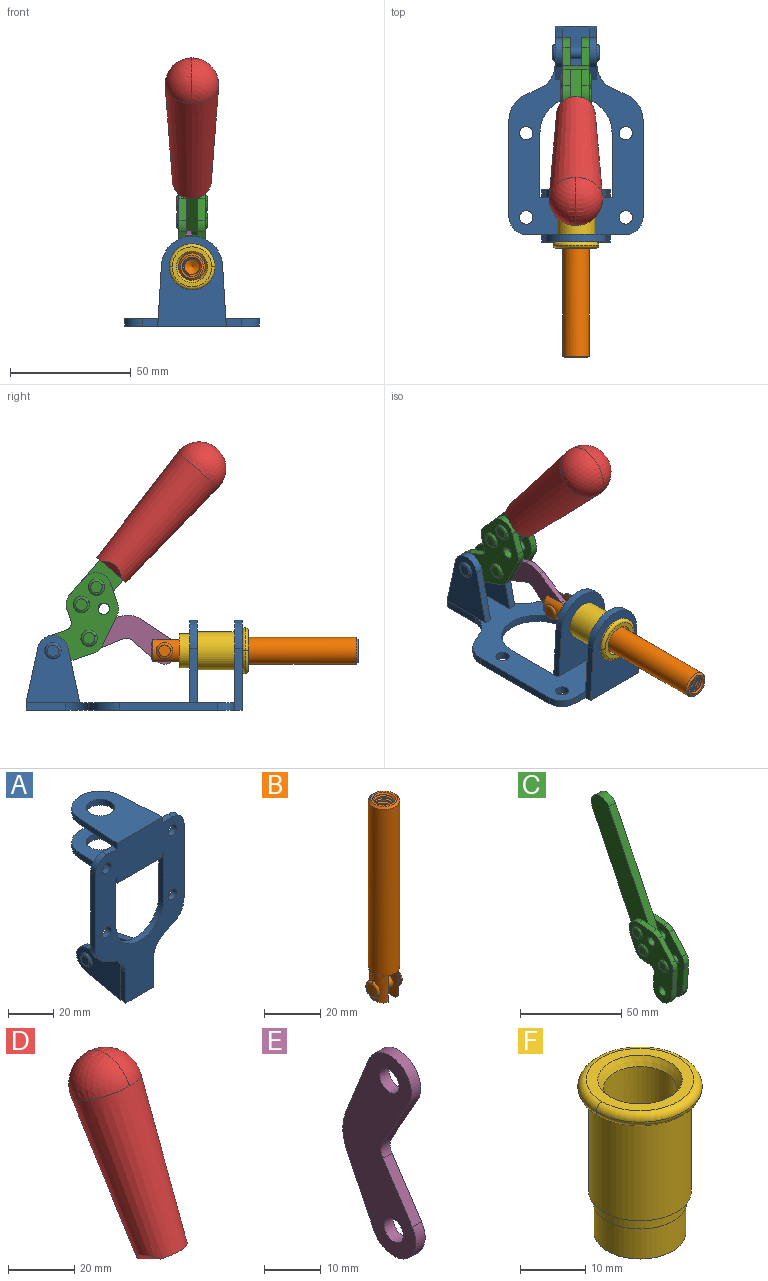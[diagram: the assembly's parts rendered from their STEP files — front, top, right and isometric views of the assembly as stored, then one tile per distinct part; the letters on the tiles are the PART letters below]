
ASSEMBLY  parts=6 mates=6
PART A: 55 faces, bbox 55.7x37.4x89.8 mm
  f0: torus R=2.41mm, axis (-1,0,0), area 15mm2, adj f11,f15,f25
  f1: torus R=2.41mm, axis (-1,0,0), area 15mm2, adj f10,f12,f22
  f2: cylinder r=2.78mm len=5.56mm, axis (0,-1,0), area 54.2mm2, adj f30,f54
  f3: cylinder r=14.99mm len=29.97mm, axis (0,-1,0), area 145.9mm2, adj f30,f49,f53,f54
  f4: cylinder r=2.78mm len=5.56mm, axis (0,-1,0), area 54.2mm2, adj f30,f54
  f5: cylinder r=2.78mm len=5.56mm, axis (0,-1,0), area 54.2mm2, adj f30,f54
  f6: cylinder r=2.78mm len=5.56mm, axis (0,-1,0), area 54.2mm2, adj f30,f54
  f7: cylinder r=6.35mm len=12.7mm, axis (0,0,1), area 123.6mm2, adj f27,f51
  f8: cylinder r=6.35mm len=12.7mm, axis (0,0,-1), area 124.7mm2, adj f21,f35
  f9: cylinder r=2.41mm len=11.18mm, axis (-1,0,0), area 169.4mm2, adj f16,f19
  f10: plane 4.83x4.83mm, normal (1,0,0), area 18.3mm2, adj f1,f12
  f11: plane 4.83x4.83mm, normal (-1,0,0), area 18.3mm2, adj f0,f15
  f12: torus R=2.41mm, axis (-1,0,0), area 15mm2, adj f1,f10,f22
  f13: cylinder r=6.35mm len=12.41mm, axis (1,0,0), area 53.4mm2, adj f18,f19,f22,f23
  f14: cylinder r=6.35mm len=12.41mm, axis (-1,0,0), area 53.4mm2, adj f16,f17,f24,f25
  f15: torus R=2.41mm, axis (-1,0,0), area 15mm2, adj f0,f11,f25
  f16: plane 27.86x22.35mm, normal (1,0,0), area 425.4mm2, adj f9,f14,f17,f24,f30
  f17: plane 22.86x4.97mm, normal (0,0.21,0.98), area 72.5mm2, adj f14,f16,f25,f30
  f18: plane 22.86x4.97mm, normal (0,0.21,0.98), area 72.5mm2, adj f13,f19,f22,f30
  f19: plane 27.86x22.35mm, normal (-1,0,0), area 425.4mm2, adj f9,f13,f18,f23,f30
  f20: cylinder r=12.7mm len=25.35mm, axis (0,0,-1), area 119.8mm2, adj f21,f34,f35,f36
  f21: plane 34.21x28.07mm, normal (0,0,-1), area 702.4mm2, adj f8,f20,f30,f34,f36
  f22: plane 27.96x22.45mm, normal (1,0,0), area 407.2mm2, adj f1,f12,f13,f18,f23,f30,f42,f43
  f23: plane 22.86x4.97mm, normal (0,0.21,-0.98), area 72.5mm2, adj f13,f19,f22,f44
  f24: plane 22.86x4.97mm, normal (0,0.21,-0.98), area 72.5mm2, adj f14,f16,f25,f44
  f25: plane 27.86x22.35mm, normal (-1,0,0), area 407.1mm2, adj f0,f14,f15,f17,f24,f30,f45,f46
  f26: plane 3.1x0.95mm, normal (0,0,-1), area 2.7mm2, adj f30,f49,f50,f54
  f27: plane 34.21x28.07mm, normal (0,0,1), area 702.4mm2, adj f7,f28,f30,f50,f52
  f28: cylinder r=12.7mm len=25.35mm, axis (0,0,1), area 118.8mm2, adj f27,f50,f51,f52
  f29: plane 3.1x0.95mm, normal (0,0,-1), area 2.7mm2, adj f30,f52,f53,f54
  f30: plane 86.54x55.63mm, normal (0,1,0), area 2362.9mm2, adj f2,f3,f4,f5,f6,f16,f17,f18
  f31: plane 40.56x3.1mm, normal (-1,0,0), area 125.7mm2, adj f30,f32,f48,f54
  f32: cylinder r=7.11mm len=7.11mm, axis (0,-1,0), area 34.6mm2, adj f30,f31,f33,f54
  f33: plane 6.67x3.1mm, normal (0,0,1), area 20.4mm2, adj f30,f32,f34,f54
  f34: plane 25.39x3.13mm, normal (-1,0.06,0), area 79.5mm2, adj f20,f21,f33,f35,f54
  f35: plane 37.31x28.45mm, normal (0,0,1), area 789.9mm2, adj f8,f20,f34,f36,f54
  f36: plane 25.39x3.13mm, normal (1,0.06,0), area 79.5mm2, adj f20,f21,f35,f37,f54
  f37: plane 6.67x3.1mm, normal (0,0,1), area 20.4mm2, adj f30,f36,f38,f54
  f38: cylinder r=7.11mm len=7.11mm, axis (0,-1,0), area 34.6mm2, adj f30,f37,f39,f54
  f39: plane 40.56x3.1mm, normal (1,0,0), area 125.7mm2, adj f30,f38,f40,f54
  f40: cylinder r=11.18mm len=10.16mm, axis (0,-1,0), area 39.5mm2, adj f30,f39,f41,f54
  f41: plane 6.09x3.1mm, normal (0.42,0,-0.91), area 20.8mm2, adj f30,f40,f42,f54
  f42: cylinder r=11.18mm len=9.41mm, axis (0,-1,0), area 37.2mm2, adj f22,f30,f41,f43,f54
  f43: plane 16.5x3.1mm, normal (1,0,0), area 51.1mm2, adj f22,f42,f44,f54
  f44: plane 17.37x3.1mm, normal (0,0,-1), area 53.8mm2, adj f23,f24,f30,f43,f45,f54
  f45: plane 16.5x3.1mm, normal (-1,0,0), area 51.1mm2, adj f25,f44,f46,f54
  f46: cylinder r=11.18mm len=9.41mm, axis (0,-1,0), area 37.2mm2, adj f25,f30,f45,f47,f54
  f47: plane 6.09x3.1mm, normal (-0.42,0,-0.91), area 20.8mm2, adj f30,f46,f48,f54
  f48: cylinder r=11.18mm len=10.16mm, axis (0,-1,0), area 39.5mm2, adj f30,f31,f47,f54
  f49: plane 26.54x3.1mm, normal (-1,0,0), area 82.3mm2, adj f3,f26,f30,f54
  f50: plane 25.39x3.1mm, normal (1,0.06,0), area 78.8mm2, adj f26,f27,f28,f51,f54
  f51: plane 37.31x28.45mm, normal (0,0,-1), area 789.9mm2, adj f7,f28,f50,f52,f54
  f52: plane 25.39x3.1mm, normal (-1,0.06,0), area 78.8mm2, adj f27,f28,f29,f51,f54
  f53: plane 26.54x3.1mm, normal (1,0,0), area 82.3mm2, adj f3,f29,f30,f54
  f54: plane 89.66x55.63mm, normal (0,-1,0), area 2678.5mm2, adj f2,f3,f4,f5,f6,f26,f29,f31
PART B: 48 faces, bbox 12.6x11.1x86.1 mm
  f0: torus R=2.41mm, axis (-1,0,0), area 15mm2, adj f30,f32,f34
  f1: torus R=2.41mm, axis (-1,0,0), area 15mm2, adj f29,f31,f33
  f2: cylinder r=5.54mm len=72.39mm, axis (0,0,1), area 2518.5mm2, adj f3,f4,f42,f43
  f3: cone r=5.54mm half-angle=45deg, axis (0,0,1), area 7.6mm2, adj f2,f5,f41
  f4: cone r=5.54mm half-angle=45deg, axis (0,0,-1), area 34.9mm2, adj f2,f39
  f5: cylinder r=5.08mm len=11.48mm, axis (0,0,1), area 108.3mm2, adj f3,f7,f8,f41
  f6: cylinder r=2.41mm len=4.83mm, axis (-1,0,0), area 71.2mm2, adj f40,f41
  f7: cylinder r=2.41mm len=4.83mm, axis (-1,0,0), area 7.6mm2, adj f5,f34
  f8: cone r=5.08mm half-angle=45deg, axis (0,0,1), area 10.6mm2, adj f5,f37,f41
  f9: cone r=3.98mm half-angle=45deg, axis (0,0,1), area 17.6mm2, adj f27,f39,f45,f46,f47
  f10: cylinder r=2.41mm len=4.83mm, axis (-1,0,0), area 7.6mm2, adj f33,f38
  f11: cylinder r=3.2mm len=6.4mm, axis (0,0,1), area 78.4mm2, adj f12,f28,f44,f45,f47
  f12: cylinder r=3.2mm len=6.4mm, axis (0,0,1), area 10.5mm2, adj f11,f13,f45,f47
  f13: cylinder r=3.2mm len=6.4mm, axis (0,0,1), area 10.5mm2, adj f12,f14,f45,f47
  f14: cylinder r=3.2mm len=6.4mm, axis (0,0,1), area 10.5mm2, adj f13,f15,f45,f47
  f15: cylinder r=3.2mm len=6.4mm, axis (0,0,1), area 10.5mm2, adj f14,f16,f45,f47
  f16: cylinder r=3.2mm len=6.4mm, axis (0,0,1), area 10.5mm2, adj f15,f17,f45,f47
  f17: cylinder r=3.2mm len=6.4mm, axis (0,0,1), area 10.5mm2, adj f16,f18,f45,f47
  f18: cylinder r=3.2mm len=6.4mm, axis (0,0,1), area 10.5mm2, adj f17,f19,f45,f47
  f19: cylinder r=3.2mm len=6.4mm, axis (0,0,1), area 10.5mm2, adj f18,f20,f45,f47
  f20: cylinder r=3.2mm len=6.4mm, axis (0,0,1), area 10.5mm2, adj f19,f21,f45,f47
  f21: cylinder r=3.2mm len=6.4mm, axis (0,0,1), area 10.5mm2, adj f20,f22,f45,f47
  f22: cylinder r=3.2mm len=6.4mm, axis (0,0,1), area 10.5mm2, adj f21,f23,f45,f47
  f23: cylinder r=3.2mm len=6.4mm, axis (0,0,1), area 10.5mm2, adj f22,f24,f45,f47
  f24: cylinder r=3.2mm len=6.4mm, axis (0,0,1), area 10.5mm2, adj f23,f25,f45,f47
  f25: cylinder r=3.2mm len=6.4mm, axis (0,0,1), area 10.5mm2, adj f24,f26,f45,f47
  f26: cylinder r=3.2mm len=6.4mm, axis (0,0,1), area 10.5mm2, adj f25,f27,f45,f47
  f27: cylinder r=3.2mm len=6.4mm, axis (0,0,1), area 7.4mm2, adj f9,f26,f45,f47
  f28: cone r=3.2mm half-angle=60deg, axis (0,0,1), area 37.2mm2, adj f11
  f29: plane 4.83x4.83mm, normal (-1,0,0), area 18.3mm2, adj f1,f31
  f30: plane 4.83x4.83mm, normal (1,0,0), area 18.3mm2, adj f0,f32
  f31: torus R=2.41mm, axis (-1,0,0), area 15mm2, adj f1,f29,f33
  f32: torus R=2.41mm, axis (-1,0,0), area 15mm2, adj f0,f30,f34
  f33: plane 6.83x6.83mm, normal (1,0,0), area 18.3mm2, adj f1,f10,f31
  f34: plane 6.83x6.83mm, normal (-1,0,0), area 18.3mm2, adj f0,f7,f32
  f35: cone r=5.08mm half-angle=45deg, axis (0,0,1), area 10.6mm2, adj f36,f38,f40
  f36: plane 7.25x1.97mm, normal (0,0,-1), area 10mm2, adj f35,f40
  f37: plane 7.25x1.97mm, normal (0,0,-1), area 10mm2, adj f8,f41
  f38: cylinder r=5.08mm len=11.48mm, axis (0,0,1), area 108.3mm2, adj f10,f35,f40,f42
  f39: plane 9.55x9.55mm, normal (0,0,1), area 22mm2, adj f4,f9
  f40: plane 12.76x10.09mm, normal (1,0,0), area 95.7mm2, adj f6,f35,f36,f38,f42,f43
  f41: plane 12.76x10.09mm, normal (-1,0,0), area 95.7mm2, adj f3,f5,f6,f8,f37,f43
  f42: cone r=5.54mm half-angle=45deg, axis (0,0,1), area 7.6mm2, adj f2,f38,f40
  f43: plane 11.07x4.7mm, normal (0,0,-1), area 50.4mm2, adj f2,f40,f41
  f44: plane 0.89x0.62mm, normal (-1,0,0), area 0.3mm2, adj f11,f45,f46,f47
  f45: bspline ~24.8x7.63mm, area 266.6mm2, adj f9,f11,f12,f13,f14,f15,f16,f17
  f46: bspline ~24.87x7.63mm, area 73.6mm2, adj f9,f44,f45,f47
  f47: bspline ~24.98x7.63mm, area 272.5mm2, adj f9,f11,f12,f13,f14,f15,f16,f17
PART C: 59 faces, bbox 12.9x60.2x99.6 mm
  f0: torus R=2.39mm, axis (-1,0,0), area 14.9mm2, adj f20,f43,f51
  f1: torus R=2.39mm, axis (-1,0,0), area 14.9mm2, adj f19,f42,f51
  f2: torus R=2.39mm, axis (-1,0,0), area 14.9mm2, adj f18,f35,f51
  f3: torus R=2.39mm, axis (-1,0,0), area 14.9mm2, adj f14,f17,f23
  f4: torus R=2.39mm, axis (-1,0,0), area 14.9mm2, adj f13,f16,f23
  f5: torus R=2.39mm, axis (-1,0,0), area 14.9mm2, adj f12,f15,f23
  f6: cylinder r=2.39mm len=4.78mm, axis (1,0,0), area 46.5mm2, adj f48,f50,f51
  f7: cylinder r=2.39mm len=4.78mm, axis (1,0,0), area 46.5mm2, adj f50,f51
  f8: cylinder r=6.35mm len=12.68mm, axis (1,0,0), area 61.8mm2, adj f38,f39,f50,f51
  f9: cylinder r=2.39mm len=4.78mm, axis (-1,0,0), area 70.5mm2, adj f46,f50
  f10: cylinder r=2.39mm len=4.78mm, axis (-1,0,0), area 46.5mm2, adj f23,f45,f46
  f11: cylinder r=2.39mm len=4.78mm, axis (-1,0,0), area 46.5mm2, adj f23,f46
  f12: plane 4.78x4.78mm, normal (1,0,0), area 17.9mm2, adj f5,f15
  f13: plane 4.78x4.78mm, normal (1,0,0), area 17.9mm2, adj f4,f16
  f14: plane 4.78x4.78mm, normal (1,0,0), area 17.9mm2, adj f3,f17
  f15: torus R=2.39mm, axis (-1,0,0), area 14.9mm2, adj f5,f12,f23
  f16: torus R=2.39mm, axis (-1,0,0), area 14.9mm2, adj f4,f13,f23
  f17: torus R=2.39mm, axis (-1,0,0), area 14.9mm2, adj f3,f14,f23
  f18: plane 4.78x4.78mm, normal (-1,0,0), area 17.9mm2, adj f2,f35
  f19: plane 4.78x4.78mm, normal (-1,0,0), area 17.9mm2, adj f1,f42
  f20: plane 4.78x4.78mm, normal (-1,0,0), area 17.9mm2, adj f0,f43
  f21: plane 2.26x0.2mm, normal (1,0,0), area 0.2mm2, adj f31,f44
  f22: plane 2.26x0.2mm, normal (-1,0,0), area 0.2mm2, adj f41,f44
  f23: plane 39.37x30.77mm, normal (1,0,0), area 565.5mm2, adj f3,f4,f5,f10,f11,f15,f16,f17
  f24: cylinder r=6.1mm len=4.15mm, axis (-1,0,0), area 14.7mm2, adj f23,f25,f32,f46
  f25: plane 10.25x9.01mm, normal (0,-0.75,0.66), area 42.3mm2, adj f23,f24,f26,f46
  f26: cylinder r=6.35mm len=4.64mm, axis (-1,0,0), area 15.6mm2, adj f23,f25,f27,f46
  f27: plane 15.84x3.1mm, normal (0,-1,-0.07), area 49.2mm2, adj f23,f26,f28,f46
  f28: cylinder r=6.35mm len=12.68mm, axis (-1,0,0), area 61.8mm2, adj f23,f27,f29,f46
  f29: plane 8.11x3.1mm, normal (0,1,0.07), area 25.2mm2, adj f23,f28,f30,f46
  f30: cylinder r=3.05mm len=3.25mm, axis (-1,0,0), area 14.8mm2, adj f23,f29,f31,f46
  f31: plane 5.99x3.1mm, normal (0,0.07,-1), area 18.6mm2, adj f21,f23,f30,f44,f46
  f32: plane 9.5x3.1mm, normal (0,-0.07,1), area 29.5mm2, adj f23,f24,f33,f46,f47
  f33: cylinder r=6.1mm len=8.63mm, axis (-1,0,0), area 39.1mm2, adj f23,f32,f34,f47
  f34: plane 8.65x3.96mm, normal (0,0.91,-0.42), area 29.5mm2, adj f23,f33,f44,f47
  f35: torus R=2.39mm, axis (-1,0,0), area 14.9mm2, adj f2,f18,f51
  f36: plane 10.25x9.01mm, normal (0,-0.75,0.66), area 42.3mm2, adj f37,f49,f50,f51
  f37: cylinder r=6.35mm len=4.64mm, axis (1,0,0), area 15.6mm2, adj f36,f38,f50,f51
  f38: plane 15.84x3.1mm, normal (0,-1,-0.07), area 49.2mm2, adj f8,f37,f50,f51
  f39: plane 8.11x3.1mm, normal (0,1,0.07), area 25.2mm2, adj f8,f40,f50,f51
  f40: cylinder r=3.05mm len=3.25mm, axis (1,0,0), area 14.8mm2, adj f39,f41,f50,f51
  f41: plane 5.99x3.1mm, normal (0,0.07,-1), area 18.6mm2, adj f22,f40,f44,f50,f51
  f42: torus R=2.39mm, axis (-1,0,0), area 14.9mm2, adj f1,f19,f51
  f43: torus R=2.39mm, axis (-1,0,0), area 14.9mm2, adj f0,f20,f51
  f44: cylinder r=6.35mm len=12.12mm, axis (-1,0,0), area 128.9mm2, adj f21,f22,f23,f31,f34,f41,f46,f47
  f45: plane 2.65x1.35mm, normal (1,0,0), area 1mm2, adj f10,f55
  f46: plane 39.08x20.42mm, normal (-1,0,0), area 412.5mm2, adj f9,f10,f11,f24,f25,f26,f27,f28
  f47: plane 77.62x39.82mm, normal (1,0,0), area 850mm2, adj f32,f33,f34,f44,f53,f54,f55
  f48: plane 2.65x1.35mm, normal (-1,0,0), area 1mm2, adj f6,f55
  f49: cylinder r=6.1mm len=4.15mm, axis (1,0,0), area 14.7mm2, adj f36,f50,f51,f56
  f50: plane 39.08x20.42mm, normal (1,0,0), area 412.5mm2, adj f6,f7,f8,f9,f36,f37,f38,f39
  f51: plane 39.37x30.77mm, normal (-1,0,0), area 565.5mm2, adj f0,f1,f2,f6,f7,f8,f35,f36
  f52: plane 8.65x3.96mm, normal (0,0.91,-0.42), area 29.5mm2, adj f44,f51,f57,f58
  f53: plane 68.49x33.4mm, normal (0,0.9,-0.44), area 358.1mm2, adj f44,f47,f54,f58
  f54: cylinder r=6.35mm len=12.06mm, axis (1,0,0), area 93.7mm2, adj f47,f53,f55,f58
  f55: plane 68.49x33.4mm, normal (0,-0.9,0.44), area 358.1mm2, adj f44,f45,f46,f47,f48,f50,f54,f58
  f56: plane 9.5x3.1mm, normal (0,-0.07,1), area 29.5mm2, adj f49,f50,f51,f57,f58
  f57: cylinder r=6.1mm len=8.63mm, axis (1,0,0), area 39.1mm2, adj f51,f52,f56,f58
  f58: plane 77.62x39.82mm, normal (-1,0,0), area 850mm2, adj f44,f52,f53,f54,f55,f56,f57
PART D: 11 faces, bbox 22.3x42.6x64.5 mm
  f0: sphere r=11.13mm, area 411.4mm2, adj f1,f8
  f1: cone r=11.11mm half-angle=3.3deg, axis (0,0.44,0.9), area 3251.8mm2, adj f0,f7,f8,f9,f10
  f2: cylinder r=6.16mm len=11.7mm, axis (1,0,0), area 89.5mm2, adj f3,f4,f5,f6
  f3: plane 60.23x36.75mm, normal (-1,0,0), area 763.6mm2, adj f2,f4,f6,f10
  f4: plane 51.37x25.05mm, normal (0,0.9,-0.44), area 264.2mm2, adj f2,f3,f5,f10
  f5: plane 60.23x36.75mm, normal (1,0,0), area 763.6mm2, adj f2,f4,f6,f10
  f6: plane 51.37x25.05mm, normal (0,-0.9,0.44), area 264.2mm2, adj f2,f3,f5,f10
  f7: plane 9.95x5.95mm, normal (0.71,-0.31,-0.64), area 25.8mm2, adj f1,f10
  f8: sphere r=11.13mm, area 411.4mm2, adj f0,f1
  f9: plane 9.95x5.95mm, normal (-0.71,-0.31,-0.64), area 25.8mm2, adj f1,f10
  f10: plane 14.27x11.38mm, normal (0,-0.44,-0.9), area 106.7mm2, adj f1,f3,f4,f5,f6,f7,f9
PART E: 12 faces, bbox 2.3x18.2x42.8 mm
  f0: cylinder r=2.4mm len=4.8mm, axis (1,0,0), area 34.9mm2, adj f4,f11
  f1: cylinder r=10.41mm len=8.47mm, axis (1,0,0), area 20.2mm2, adj f4,f9,f10,f11
  f2: cylinder r=3.05mm len=3.16mm, axis (1,0,0), area 7.7mm2, adj f4,f6,f7,f11
  f3: cylinder r=2.4mm len=4.8mm, axis (1,0,0), area 34.9mm2, adj f4,f11
  f4: plane 42.81x18.23mm, normal (-1,0,0), area 414.1mm2, adj f0,f1,f2,f3,f5,f6,f7,f8
  f5: cylinder r=5.54mm len=10.67mm, axis (1,0,0), area 41.8mm2, adj f4,f6,f10,f11
  f6: plane 11.66x6.53mm, normal (0,-0.87,-0.49), area 30.9mm2, adj f2,f4,f5,f11
  f7: plane 11.17x7.33mm, normal (0,-0.84,0.55), area 30.9mm2, adj f2,f4,f8,f11
  f8: cylinder r=5.54mm len=10.51mm, axis (1,0,0), area 41.8mm2, adj f4,f7,f9,f11
  f9: plane 13.67x6.67mm, normal (0,0.9,-0.44), area 35.1mm2, adj f1,f4,f8,f11
  f10: plane 14.1x5.7mm, normal (0,0.93,0.37), area 35.1mm2, adj f1,f4,f5,f11
  f11: plane 42.81x18.23mm, normal (1,0,0), area 414.1mm2, adj f0,f1,f2,f3,f5,f6,f7,f8
PART F: 15 faces, bbox 20.6x20.6x28.7 mm
  f0: torus R=8.26mm, axis (0,0,1), area 56.8mm2, adj f1,f10,f12
  f1: torus R=8.26mm, axis (0,0,1), area 56.8mm2, adj f0,f6,f13
  f2: cylinder r=5.59mm len=25.91mm, axis (0,0,1), area 909.6mm2, adj f3,f4
  f3: cone r=6.86mm half-angle=45deg, axis (0,0,-1), area 70.2mm2, adj f2,f14
  f4: cone r=6.47mm half-angle=30deg, axis (0,0,1), area 66.7mm2, adj f2,f13
  f5: cylinder r=7.04mm len=14.07mm, axis (0,0,1), area 252.6mm2, adj f11,f14
  f6: torus R=8.26mm, axis (0,0,1), area 56.8mm2, adj f1,f12,f13
  f7: cylinder r=7.16mm len=14.33mm, axis (0,0,1), area 91.5mm2, adj f9,f11
  f8: cylinder r=7.86mm len=18.42mm, axis (0,0,1), area 909.6mm2, adj f9,f10
  f9: plane 15.72x15.72mm, normal (0,0,-1), area 33mm2, adj f7,f8
  f10: plane 16.51x16.51mm, normal (0,0,-1), area 19.9mm2, adj f0,f8,f12
  f11: plane 14.33x14.33mm, normal (0,0,-1), area 5.7mm2, adj f5,f7
  f12: torus R=8.26mm, axis (0,0,1), area 56.8mm2, adj f0,f6,f10
  f13: plane 16.51x16.51mm, normal (0,0,1), area 82.7mm2, adj f1,f4,f6
  f14: plane 14.07x14.07mm, normal (0,0,-1), area 7.8mm2, adj f3,f5
PLACE A rot(axis=(1,0,0),90deg) t=(0,9.14,0)mm fixed
PLACE B rot(axis=(1,0,0),90deg) t=(0,10.38,0)mm
PLACE C rot(axis=(1,0,0),66.9deg) t=(0,2.06,14.56)mm
PLACE D rot(axis=(1,0,0),66.9deg) t=(-0.04,2.06,14.56)mm
PLACE E rot(axis=(1,0,0),101.4deg) t=(-1.16,14.95,3.55)mm
PLACE F rot(axis=(1,0,0),90deg) t=(0,9.14,0)mm
MATE fastened F.f0 <-> A.f7  axis (0,1,0) through (0,-37.25,24.61)mm
MATE revolute E.f3 <-> C.f4  axis (1,0,0) through (0,26.23,29.8)mm
MATE slider B.f2 <-> F.f2  axis (0,-1,0) through (0,-48.4,24.61)mm
MATE revolute C.f7 <-> A.f0  axis (-1,0,0) through (0,41.23,24.61)mm
MATE fastened D.f2 <-> C.f54  axis (1,0,0) through (-2.35,-20.47,101.39)mm
MATE revolute E.f5 <-> B.f6  axis (1,0,0) through (0,-5.09,24.61)mm
